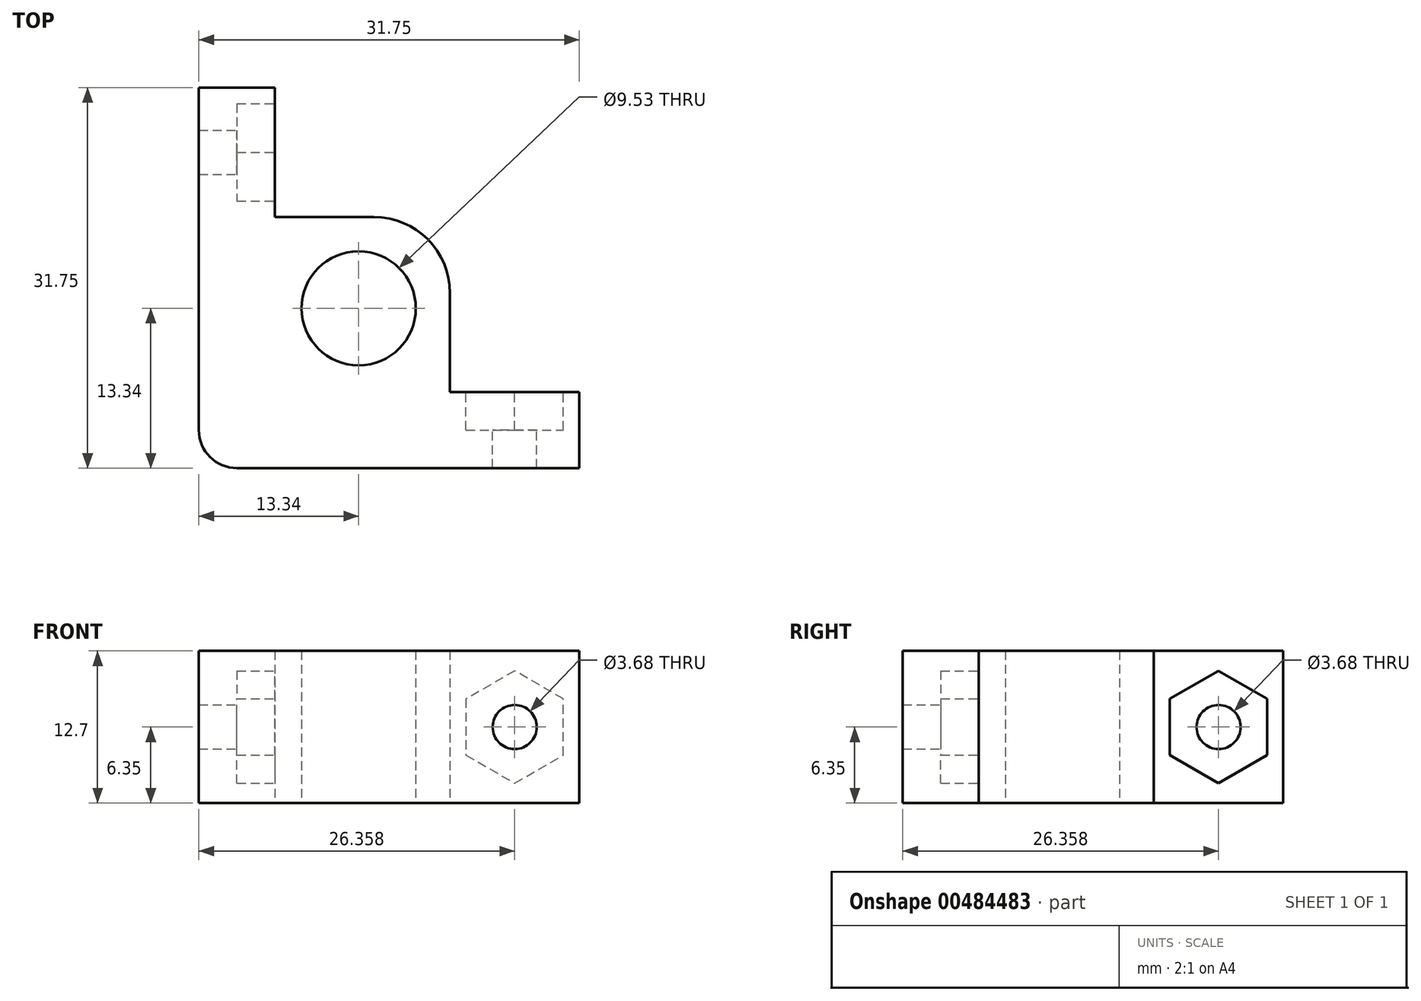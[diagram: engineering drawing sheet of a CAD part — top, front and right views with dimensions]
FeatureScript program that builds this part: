
annotation { "Feature Type Name" : "Feature", "Feature Type Description" : "" }
export const myFeature = defineFeature(function(context is Context, id is Id, definition is map)
    precondition{}
    {
        {
            var Q0;
            Q0=qCreatedBy(makeId("Top.planeOp"),FACE);
            var sketch = newSketch(context, id + "F0", { "sketchPlane" : qUnion([Q0])});
            skCircle(sketch, "E0", {"center": v(0, 0) * mm, "radius": 4.76 * mm});
            skLineSegment(sketch, "E1", {"start": v(-13.33, -13.34) * mm, "end": v(18.41, -13.34) * mm});
            skLineSegment(sketch, "E2", {"start": v(18.41, -13.34) * mm, "end": v(18.41, -6.99) * mm});
            skLineSegment(sketch, "E3", {"start": v(18.41, -6.98) * mm, "end": v(7.62, -6.99) * mm});
            skLineSegment(sketch, "E4", {"start": v(7.62, -6.99) * mm, "end": v(7.62, 7.62) * mm});
            skLineSegment(sketch, "E5", {"start": v(7.62, 7.62) * mm, "end": v(-6.99, 7.62) * mm});
            skLineSegment(sketch, "E6", {"start": v(-6.99, 7.62) * mm, "end": v(-6.99, 18.41) * mm});
            skLineSegment(sketch, "E7", {"start": v(-6.99, 18.41) * mm, "end": v(-13.34, 18.41) * mm});
            skLineSegment(sketch, "E8", {"start": v(-13.34, 18.41) * mm, "end": v(-13.33, -13.34) * mm});
            skSolve(sketch);
        }
        {
            var Q0;
            Q0 = qSketchRegion(id + "F0", true);
            extrude(context, id + "F1", {"entities" : qUnion([Q0]), "depth" : 12.7 * mm, "offsetDistance" : 25.4 * mm});
        }
        {
            var Q0;
            Q0=makeQuery(id+"F1.opExtrude","SWEPT_EDGE",EDGE,{"disambiguationData":[OSD([sQuery(id+"F0.wireOp",EDGE,"E4"),sQuery(id+"F0.wireOp",EDGE,"E5")])]});
            fillet(context, id + "F2", {"entities" : qUnion([Q0]), "radius" : 6.35 * mm, "tangentPropagation" : true, "allowEdgeOverflow" : false});
        }
        {
            var Q0;
            Q0=makeQuery(id+"F1.opExtrude","SWEPT_EDGE",EDGE,{"disambiguationData":[OSD([sQuery(id+"F0.wireOp",EDGE,"E1"),sQuery(id+"F0.wireOp",EDGE,"E8")])]});
            fillet(context, id + "F3", {"entities" : qUnion([Q0]), "radius" : 3.17 * mm, "tangentPropagation" : true, "allowEdgeOverflow" : false});
        }
        {
            var Q0;
            Q0=makeQuery(id+"F1.opExtrude","SWEPT_FACE",FACE,{"disambiguationData":[OSD([sQuery(id+"F0.wireOp",EDGE,"E3")])]});
            var sketch = newSketch(context, id + "F4", { "sketchPlane" : qUnion([Q0])});
            skCircle(sketch, "E9", {"center": v(-13.02, 6.35) * mm, "radius": 1.84 * mm});
            skPoint(sketch, "E9.centerSnap0", {"position": v(-18.41, 6.35) * mm});
            skPoint(sketch, "E9.centerSnap1", {"position": v(-13.02, 0) * mm});
            skSolve(sketch);
        }
        {
            var Q0;
            Q0 = qSketchRegion(id + "F4", true);
            extrude(context, id + "F5", {"entities" : qUnion([Q0]), "operationType" : NewBodyOperationType.REMOVE, "oppositeDirection" : true, "depth" : 25.4 * mm, "offsetDistance" : 25.4 * mm});
        }
        {
            var Q0;
            Q0=makeQuery(id+"F1.opExtrude","SWEPT_FACE",FACE,{"disambiguationData":[OSD([sQuery(id+"F0.wireOp",EDGE,"E3")])]});
            var sketch = newSketch(context, id + "F6", { "sketchPlane" : qUnion([Q0])});
            skCircle(sketch, "E10.cCircle", {"center": v(-13.02, 6.35) * mm, "radius": 4.06 * mm, "construction": true});
            skLineSegment(sketch, "E10.0", {"start": v(-13.02, 1.66) * mm, "end": v(-17.08, 4) * mm});
            skLineSegment(sketch, "E10.1", {"start": v(-17.08, 4) * mm, "end": v(-17.08, 8.7) * mm});
            skLineSegment(sketch, "E10.2", {"start": v(-17.08, 8.7) * mm, "end": v(-13.02, 11.04) * mm});
            skLineSegment(sketch, "E10.3", {"start": v(-13.02, 11.04) * mm, "end": v(-8.95, 8.7) * mm});
            skLineSegment(sketch, "E10.4", {"start": v(-8.95, 8.7) * mm, "end": v(-8.95, 4) * mm});
            skLineSegment(sketch, "E10.5", {"start": v(-8.95, 4) * mm, "end": v(-13.02, 1.66) * mm});
            skPoint(sketch, "E10.0.midPoint", {"position": v(-15.05, 2.83) * mm});
            skSolve(sketch);
        }
        {
            var Q0;
            Q0 = qSketchRegion(id + "F6", true);
            extrude(context, id + "F7", {"entities" : qUnion([Q0]), "operationType" : NewBodyOperationType.REMOVE, "oppositeDirection" : true, "depth" : 3.17 * mm, "offsetDistance" : 25.4 * mm});
        }
        {
            var Q0;
            Q0=makeQuery(id+"F1.opExtrude","SWEPT_FACE",FACE,{"disambiguationData":[OSD([sQuery(id+"F0.wireOp",EDGE,"E6")])]});
            var sketch = newSketch(context, id + "F8", { "sketchPlane" : qUnion([Q0])});
            skCircle(sketch, "E11", {"center": v(13.02, 6.35) * mm, "radius": 1.84 * mm});
            skPoint(sketch, "E11.centerSnap0", {"position": v(13.02, 12.7) * mm});
            skPoint(sketch, "E11.centerSnap1", {"position": v(18.41, 6.35) * mm});
            skSolve(sketch);
        }
        {
            var Q0;
            Q0 = qSketchRegion(id + "F8", true);
            extrude(context, id + "F9", {"entities" : qUnion([Q0]), "operationType" : NewBodyOperationType.REMOVE, "oppositeDirection" : true, "depth" : 25.4 * mm, "offsetDistance" : 25.4 * mm});
        }
        {
            var Q0;
            Q0=makeQuery(id+"F1.opExtrude","SWEPT_FACE",FACE,{"disambiguationData":[OSD([sQuery(id+"F0.wireOp",EDGE,"E6")])]});
            var sketch = newSketch(context, id + "F10", { "sketchPlane" : qUnion([Q0])});
            skCircle(sketch, "E12.cCircle", {"center": v(13.02, 6.35) * mm, "radius": 4.06 * mm, "construction": true});
            skLineSegment(sketch, "E12.0", {"start": v(8.95, 4) * mm, "end": v(8.95, 8.7) * mm});
            skLineSegment(sketch, "E12.1", {"start": v(8.95, 8.7) * mm, "end": v(13.02, 11.04) * mm});
            skLineSegment(sketch, "E12.2", {"start": v(13.02, 11.04) * mm, "end": v(17.08, 8.7) * mm});
            skLineSegment(sketch, "E12.3", {"start": v(17.08, 8.7) * mm, "end": v(17.08, 4) * mm});
            skLineSegment(sketch, "E12.4", {"start": v(17.08, 4) * mm, "end": v(13.02, 1.66) * mm});
            skLineSegment(sketch, "E12.5", {"start": v(13.02, 1.66) * mm, "end": v(8.95, 4) * mm});
            skPoint(sketch, "E12.0.midPoint", {"position": v(8.95, 6.35) * mm});
            skSolve(sketch);
        }
        {
            var Q0;
            Q0 = qSketchRegion(id + "F10", true);
            extrude(context, id + "F11", {"entities" : qUnion([Q0]), "operationType" : NewBodyOperationType.REMOVE, "oppositeDirection" : true, "depth" : 3.17 * mm, "offsetDistance" : 25.4 * mm});
        }
    });
